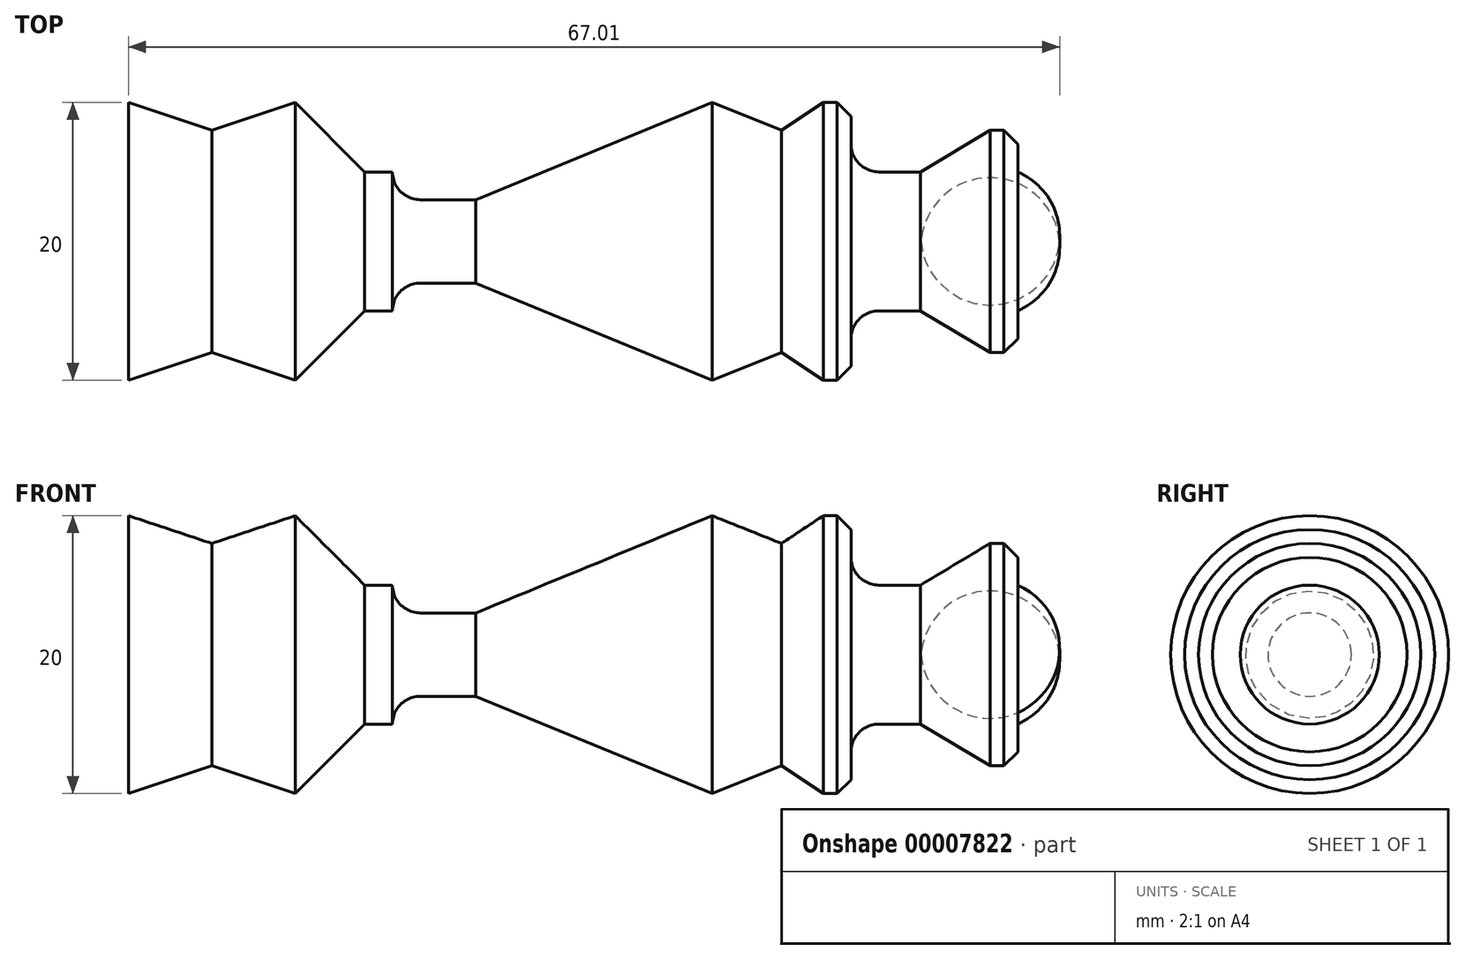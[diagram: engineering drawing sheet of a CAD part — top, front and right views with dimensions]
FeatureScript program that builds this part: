
annotation { "Feature Type Name" : "Feature", "Feature Type Description" : "" }
export const myFeature = defineFeature(function(context is Context, id is Id, definition is map)
    precondition{}
    {
        {
            var Q0;
            Q0=qCreatedBy(makeId("Front.planeOp"),FACE);
            var sketch = newSketch(context, id + "F0", { "sketchPlane" : qUnion([Q0])});
            skLineSegment(sketch, "E0", {"start": v(-40.56, 0) * mm, "end": v(46.44, 0) * mm});
            skArc(sketch, "E1", {"start": v(38.44, -5) * mm, "mid": v(40.74, -2.98) * mm, "end": v(41.44, 0) * mm});
            skLineSegment(sketch, "E2", {"start": v(38.44, -5) * mm, "end": v(38.44, -8) * mm});
            skLineSegment(sketch, "E3", {"start": v(38.44, -8) * mm, "end": v(36.44, -8) * mm});
            skLineSegment(sketch, "E4", {"start": v(36.44, -8) * mm, "end": v(31.44, -5) * mm});
            skLineSegment(sketch, "E5", {"start": v(31.44, -5) * mm, "end": v(26.44, -5) * mm});
            skLineSegment(sketch, "E6", {"start": v(26.44, -5) * mm, "end": v(26.44, -10) * mm});
            skLineSegment(sketch, "E7", {"start": v(26.44, -10) * mm, "end": v(24.44, -10) * mm});
            skLineSegment(sketch, "E8", {"start": v(24.44, -10) * mm, "end": v(21.44, -8) * mm});
            skLineSegment(sketch, "E9", {"start": v(-0.56, -3) * mm, "end": v(-6.56, -3) * mm});
            skLineSegment(sketch, "E10", {"start": v(-6.56, -3) * mm, "end": v(-6.56, -5) * mm});
            skLineSegment(sketch, "E11", {"start": v(-6.56, -5) * mm, "end": v(-8.56, -5) * mm});
            skLineSegment(sketch, "E12", {"start": v(-8.56, -5) * mm, "end": v(-13.56, -10) * mm});
            skLineSegment(sketch, "E13", {"start": v(-13.56, -10) * mm, "end": v(-19.56, -8) * mm});
            skLineSegment(sketch, "E14", {"start": v(-19.56, -8) * mm, "end": v(-25.56, -10) * mm});
            skLineSegment(sketch, "E15", {"start": v(-25.56, -10) * mm, "end": v(-25.56, 0) * mm});
            skLineSegment(sketch, "E16", {"start": v(21.44, -8) * mm, "end": v(16.44, -10) * mm});
            skLineSegment(sketch, "E17", {"start": v(16.44, -10) * mm, "end": v(-0.56, -3) * mm});
            skSolve(sketch);
        }
        {
            var Q0;
            {var subQ1=sQuery(id+"F0.wireOp",EDGE,"E1");Q0=makeQuery(id+"F0.imprint","IMPRINT",FACE,{"disambiguationData":[TD([[makeQuery(id+"F0.imprint","IMPRINT",EDGE,{"derivedFrom":subQ1}),1.0]])]});}
            var Q1;
            Q1=sQuery(id+"F0.wireOp",EDGE,"E0");
            revolve(context, id + "F1", {"entities" : qUnion([Q0]), "axis" : qUnion([Q1]), "revolveType" : RevolveType.FULL});
        }
        {
            var Q0;
            Q0=makeQuery(id+"F1.opRevolve","SWEPT_EDGE",EDGE,{"disambiguationData":[OSD([sQuery(id+"F0.wireOp",EDGE,"E2"),sQuery(id+"F0.wireOp",EDGE,"E3")])]});
            chamfer(context, id + "F2", {"entities" : qUnion([Q0]), "width" : 1 * mm});
        }
        {
            var Q0;
            Q0=makeQuery(id+"F1.opRevolve","SWEPT_EDGE",EDGE,{"disambiguationData":[OSD([sQuery(id+"F0.wireOp",EDGE,"E5"),sQuery(id+"F0.wireOp",EDGE,"E6")])]});
            fillet(context, id + "F3", {"entities" : qUnion([Q0]), "radius" : 2 * mm, "allowEdgeOverflow" : false});
        }
        {
            var Q0;
            Q0=makeQuery(id+"F1.opRevolve","SWEPT_EDGE",EDGE,{"disambiguationData":[OSD([sQuery(id+"F0.wireOp",EDGE,"E6"),sQuery(id+"F0.wireOp",EDGE,"E7")])]});
            chamfer(context, id + "F4", {"entities" : qUnion([Q0]), "width" : 1 * mm});
        }
        {
            var Q0;
            Q0=makeQuery(id+"F1.opRevolve","SWEPT_EDGE",EDGE,{"disambiguationData":[OSD([sQuery(id+"F0.wireOp",EDGE,"E9"),sQuery(id+"F0.wireOp",EDGE,"E10")])]});
            fillet(context, id + "F5", {"entities" : qUnion([Q0]), "radius" : 2 * mm, "allowEdgeOverflow" : false});
        }
    });
